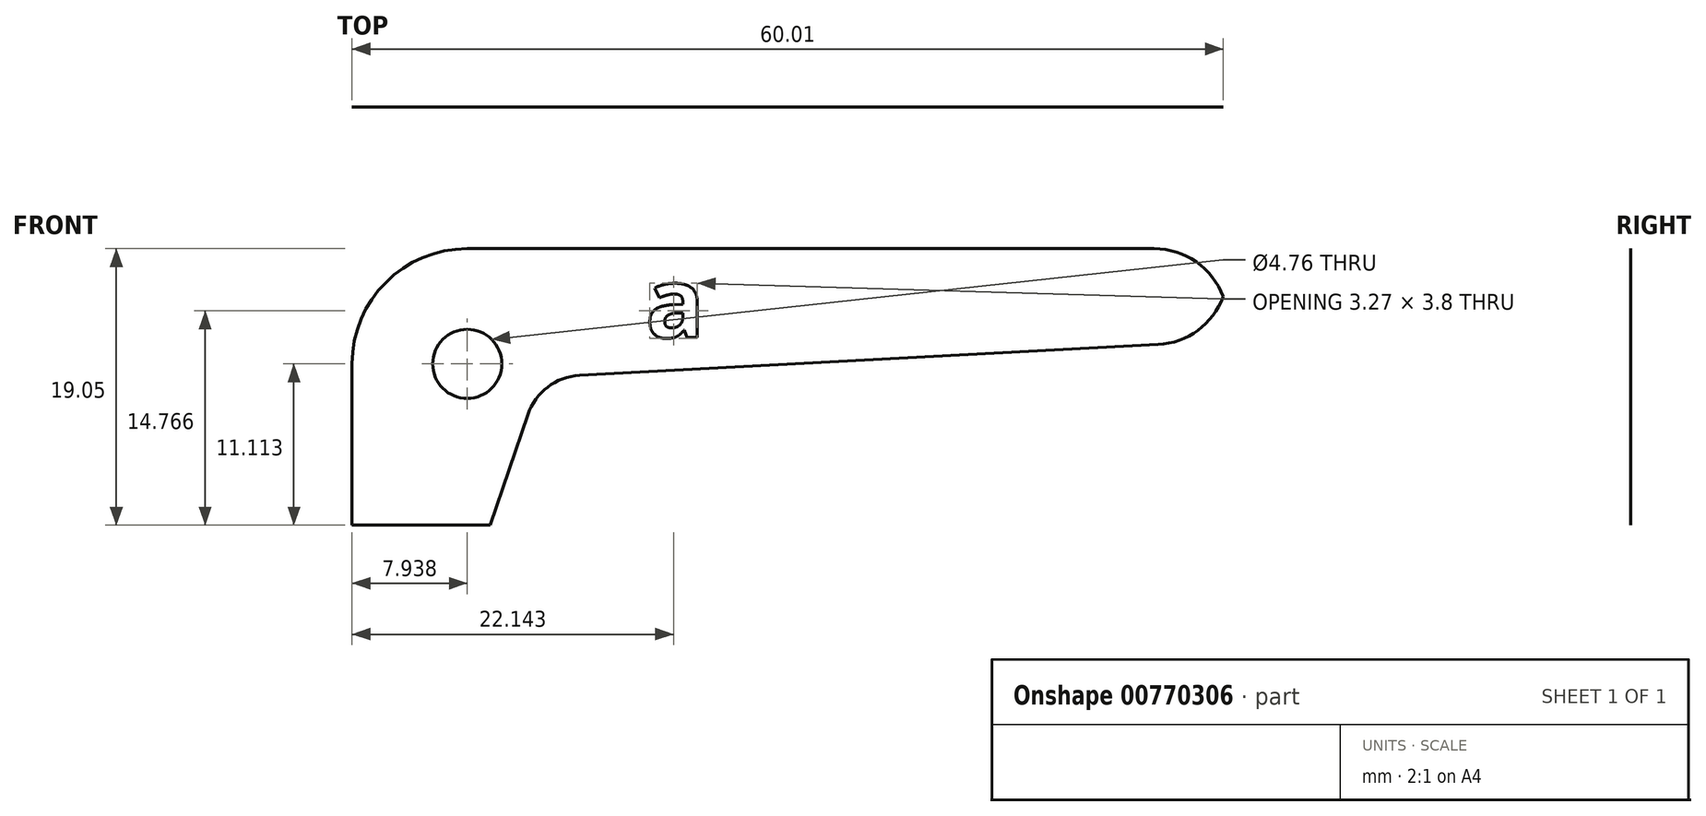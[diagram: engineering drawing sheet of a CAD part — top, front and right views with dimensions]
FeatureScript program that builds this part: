
annotation { "Feature Type Name" : "Feature", "Feature Type Description" : "" }
export const myFeature = defineFeature(function(context is Context, id is Id, definition is map)
    precondition{}
    {
        {
            var Q0;
            Q0=qCreatedBy(makeId("Front.planeOp"),FACE);
            var sketch = newSketch(context, id + "F0", { "sketchPlane" : qUnion([Q0])});
            skLineSegment(sketch, "E0.top", {"start": v(7.94, 19.05) * mm, "end": v(60.33, 19.05) * mm});
            skLineSegment(sketch, "E0.left", {"start": v(0, 0) * mm, "end": v(0, 11.11) * mm});
            skLineSegment(sketch, "E1", {"start": v(9.53, 0) * mm, "end": v(12.11, 7.63) * mm});
            skLineSegment(sketch, "E2", {"start": v(60.33, 12.7) * mm, "end": v(15.66, 10.32) * mm});
            skLineSegment(sketch, "E3", {"start": v(9.53, 0) * mm, "end": v(0, 0) * mm});
            skLineSegment(sketch, "E4", {"start": v(60.33, 19.05) * mm, "end": v(60.33, 12.7) * mm});
            skArc(sketch, "E5", {"start": v(15.66, 10.32) * mm, "mid": v(13.47, 9.52) * mm, "end": v(12.11, 7.63) * mm});
            skPoint(sketch, "E6.visualSharp", {"position": v(0, 19.05) * mm});
            skArc(sketch, "E6.filletArc", {"start": v(7.94, 19.05) * mm, "mid": v(2.32, 16.73) * mm, "end": v(0, 11.11) * mm});
            skSolve(sketch);
        }
        {
            var Q0;
            Q0=makeQuery(id+"F0.imprint","IMPRINT",FACE,{"disambiguationData":[TD([[makeQuery(id+"F0.imprint","IMPRINT",EDGE,{"derivedFrom":sQuery(id+"F0.wireOp",EDGE,"E0.top")}),-1.0]])]});
            extrude(context, id + "F1", {"entities" : qUnion([Q0]), "depth" : 3 / 812.8 * mm, "offsetDistance" : 25.4 * mm});
        }
        {
            var Q0;
            Q0=makeQuery(id+"F1.opExtrude","CAP_FACE",FACE,{"disambiguationData":[OSD([sQuery(id+"F0.wireOp",EDGE,"E0.top"),sQuery(id+"F0.wireOp",EDGE,"E0.left"),sQuery(id+"F0.wireOp",EDGE,"E1"),sQuery(id+"F0.wireOp",EDGE,"E2"),sQuery(id+"F0.wireOp",EDGE,"E3"),sQuery(id+"F0.wireOp",EDGE,"E4"),sQuery(id+"F0.wireOp",EDGE,"E5"),sQuery(id+"F0.wireOp",EDGE,"E6.filletArc")])],"isStart":false});
            var sketch = newSketch(context, id + "F2", { "sketchPlane" : qUnion([Q0])});
            skCircle(sketch, "E7", {"center": v(7.94, 11.11) * mm, "radius": 2.38 * mm});
            skSolve(sketch);
        }
        {
            var Q0;
            Q0=makeQuery(id+"F2.imprint","IMPRINT",FACE,{"disambiguationData":[TD([[makeQuery(id+"F2.imprint","IMPRINT",EDGE,{"derivedFrom":sQuery(id+"F2.wireOp",EDGE,"E7")}),1.0]])]});
            extrude(context, id + "F3", {"entities" : qUnion([Q0]), "operationType" : NewBodyOperationType.REMOVE, "oppositeDirection" : true, "depth" : 2.38 * mm, "offsetDistance" : 25.4 * mm});
        }
        {
            var Q0;
            Q0=makeQuery(id+"F1.opExtrude","SWEPT_FACE",FACE,{"disambiguationData":[OSD([sQuery(id+"F0.wireOp",EDGE,"E0.top")])]});
            var sketch = newSketch(context, id + "F4", { "sketchPlane" : qUnion([Q0])});
            skLineSegment(sketch, "E8", {"start": v(45.24, 0) * mm, "end": v(60.33, -0.8) * mm});
            skLineSegment(sketch, "E9", {"start": v(60.33, -0.8) * mm, "end": v(60.33, 0) * mm});
            skLineSegment(sketch, "E10", {"start": v(60.33, 0) * mm, "end": v(45.24, 0) * mm});
            skLineSegment(sketch, "E11.MirrorCS", {"start": v(45.24, -2.38) * mm, "end": v(60.33, -1.59) * mm});
            skSolve(sketch);
        }
        {
            var Q0;
            {var subQ0=sQuery(id+"F4.wireOp",EDGE,"E11.MirrorCS");Q0=makeQuery(id+"F4.imprint","IMPRINT",FACE,{"disambiguationData":[TD([[makeQuery(id+"F4.imprint","IMPRINT",EDGE,{"derivedFrom":subQ0}),-1.0]])]});}
            var Q1;
            Q1=makeQuery(id+"F4.imprint","IMPRINT",FACE,{"disambiguationData":[TD([[makeQuery(id+"F4.imprint","IMPRINT",EDGE,{"derivedFrom":sQuery(id+"F4.wireOp",EDGE,"E8")}),1.0]])]});
            extrude(context, id + "F5", {"entities" : qUnion([Q0, Q1]), "operationType" : NewBodyOperationType.REMOVE, "oppositeDirection" : true, "depth" : 25.4 * mm, "offsetDistance" : 25.4 * mm});
        }
        {
            var Q0;
            Q0=makeQuery(id+"F1.opExtrude","CAP_FACE",FACE,{"disambiguationData":[OSD([sQuery(id+"F0.wireOp",EDGE,"E0.top"),sQuery(id+"F0.wireOp",EDGE,"E0.left"),sQuery(id+"F0.wireOp",EDGE,"E1"),sQuery(id+"F0.wireOp",EDGE,"E2"),sQuery(id+"F0.wireOp",EDGE,"E3"),sQuery(id+"F0.wireOp",EDGE,"E4"),sQuery(id+"F0.wireOp",EDGE,"E5"),sQuery(id+"F0.wireOp",EDGE,"E6.filletArc")])],"isStart":false});
            var sketch = newSketch(context, id + "F6", { "sketchPlane" : qUnion([Q0])});
            skText(sketch, "E12", { "text": "Francisco", "fontName": "OpenSans-Bold.ttf"});
            const initialGuessF6  = {"E12": [0.0135, 0.01293, 1, 0, 0.00483]};
            skSetInitialGuess(sketch, initialGuessF6);
            skSolve(sketch);
        }
        {
            var Q0;
            Q0 = qSketchRegion(id + "F6", true);
            extrude(context, id + "F7", {"entities" : qUnion([Q0]), "operationType" : NewBodyOperationType.REMOVE, "oppositeDirection" : true, "depth" : 2.54 * mm, "offsetDistance" : 25.4 * mm});
        }
        {
            var Q0;
            Q0=makeQuery(id+"F1.opExtrude","SWEPT_EDGE",EDGE,{"disambiguationData":[OSD([sQuery(id+"F0.wireOp",EDGE,"E0.top"),sQuery(id+"F0.wireOp",EDGE,"E4")])]});
            var Q1;
            Q1=makeQuery(id+"F1.opExtrude","SWEPT_EDGE",EDGE,{"disambiguationData":[OSD([sQuery(id+"F0.wireOp",EDGE,"E2"),sQuery(id+"F0.wireOp",EDGE,"E4")])]});
            fillet(context, id + "F8", {"entities" : qUnion([Q0, Q1]), "radius" : 5.08 * mm, "tangentPropagation" : true, "allowEdgeOverflow" : false});
        }
    });
